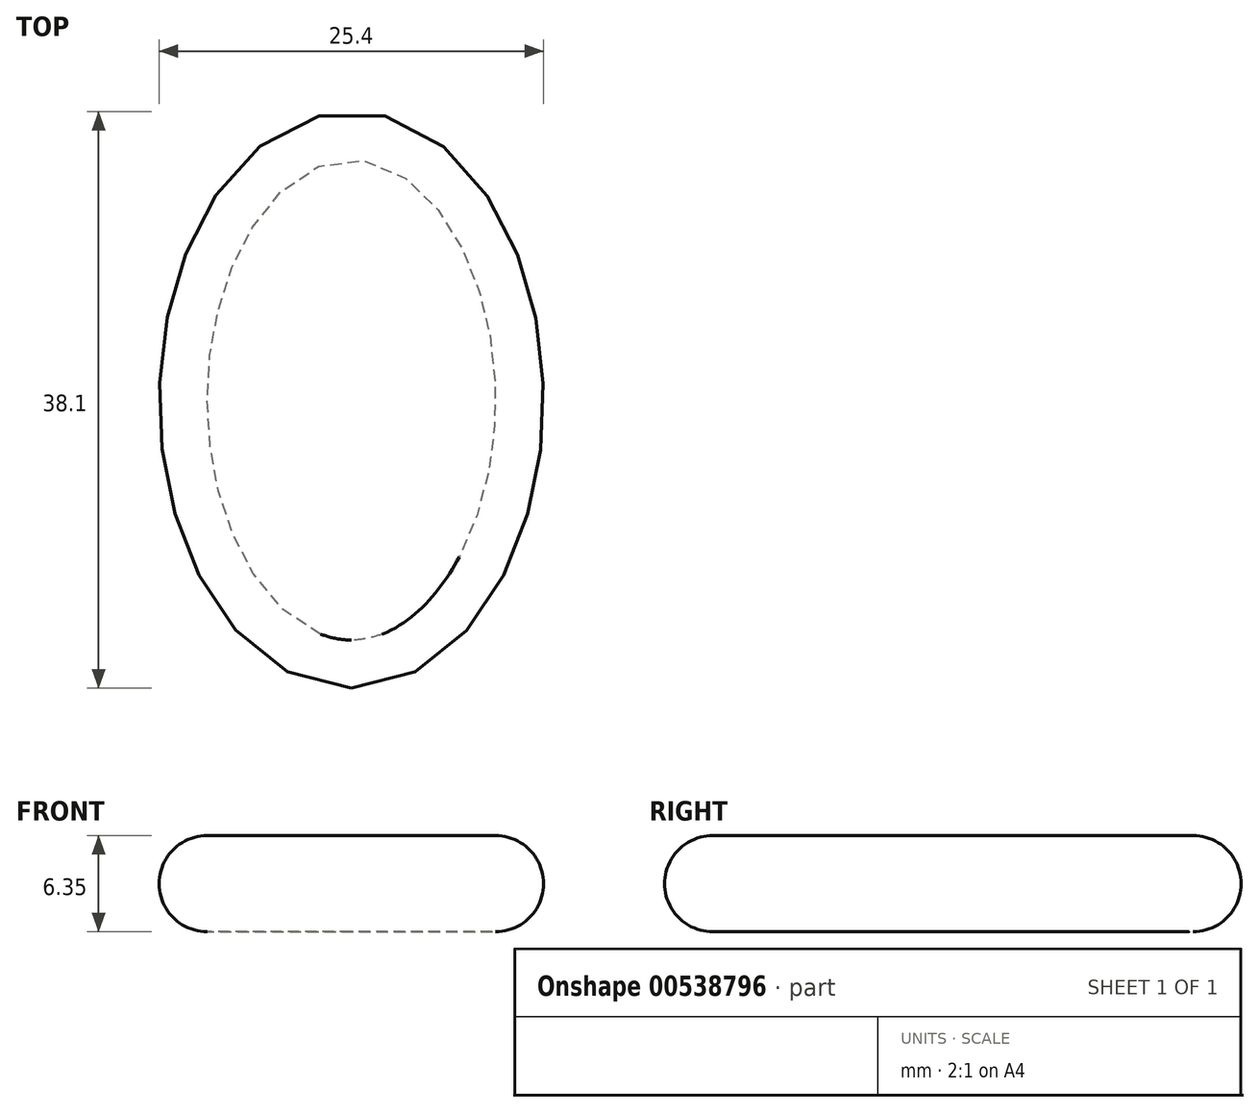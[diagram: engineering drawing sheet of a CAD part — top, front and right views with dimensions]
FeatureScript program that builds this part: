
annotation { "Feature Type Name" : "Feature", "Feature Type Description" : "" }
export const myFeature = defineFeature(function(context is Context, id is Id, definition is map)
    precondition{}
    {
        {
            var Q0;
            Q0=qCreatedBy(makeId("Top.planeOp"),FACE);
            var sketch = newSketch(context, id + "F0", { "sketchPlane" : qUnion([Q0])});
            skEllipse(sketch, "E0", {"center": v(0, 0) * mm, "majorRadius": 19.05 * mm, "minorRadius": 12.7 * mm, "majorAxis": v(0, -1)});
            skSolve(sketch);
        }
        {
            var Q0;
            Q0=makeQuery(id+"F0.imprint","IMPRINT",FACE,{"disambiguationData":[TD([[makeQuery(id+"F0.imprint","IMPRINT",EDGE,{"derivedFrom":sQuery(id+"F0.wireOp",EDGE,"E0")}),1.0]])]});
            extrude(context, id + "F1", {"entities" : qUnion([Q0]), "depth" : 6.35 * mm, "offsetDistance" : 25.4 * mm});
        }
        {
            var Q0;
            Q0=makeQuery(id+"F1.opExtrude","CAP_FACE",FACE,{"disambiguationData":[OSD([sQuery(id+"F0.wireOp",EDGE,"E0")])],"isStart":false});
            var Q1;
            Q1=makeQuery(id+"F1.opExtrude","CAP_FACE",FACE,{"disambiguationData":[OSD([sQuery(id+"F0.wireOp",EDGE,"E0")])],"isStart":true});
            fillet(context, id + "F2", {"entities" : qUnion([Q0, Q1]), "radius" : 3.17 * mm, "tangentPropagation" : true, "allowEdgeOverflow" : false});
        }
    });
